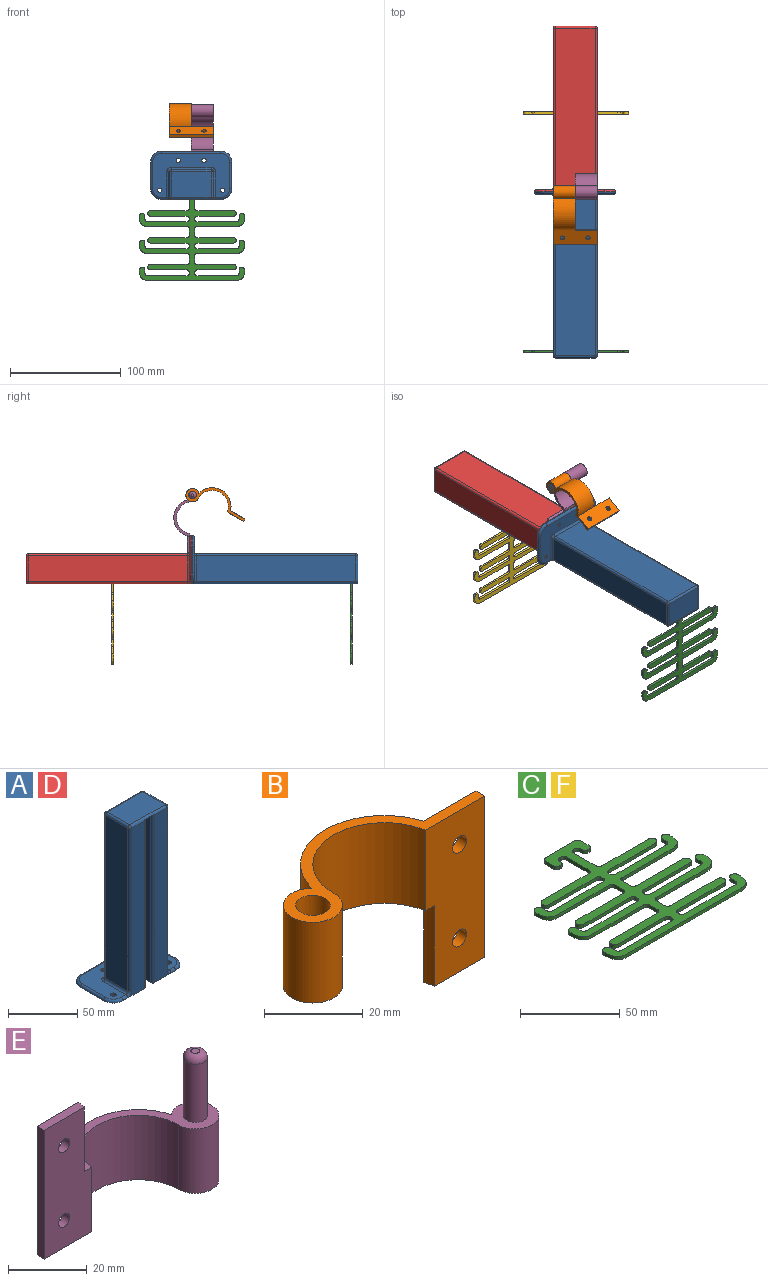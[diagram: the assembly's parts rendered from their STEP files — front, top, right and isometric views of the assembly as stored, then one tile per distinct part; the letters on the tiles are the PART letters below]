
ASSEMBLY  parts=6 mates=5
PART A: 61 faces, bbox 75.1x45.4x151.9 mm
  f0: plane 148x16.75mm, normal (0,-1,0), area 1890.4mm2, adj f16,f29,f36,f44,f47
  f1: plane 148x16.75mm, normal (0,-1,0), area 1890.4mm2, adj f16,f23,f28,f31,f36
  f2: plane 148x2mm, normal (0,1,0), area 296mm2, adj f16,f21,f54,f55
  f3: plane 148x14mm, normal (1,0,0), area 2072mm2, adj f16,f21,f55,f56
  f4: plane 148x22.5mm, normal (0,-1,0), area 3330mm2, adj f16,f21,f56,f57
  f5: plane 148x14mm, normal (-1,0,0), area 2072mm2, adj f16,f21,f57,f58
  f6: plane 148x2mm, normal (0,1,0), area 296mm2, adj f16,f21,f58,f59
  f7: plane 148x6mm, normal (1,0,0), area 888mm2, adj f16,f21,f31,f53
  f8: plane 148x2mm, normal (-1,0,0), area 296mm2, adj f16,f21,f53,f54
  f9: plane 148x2mm, normal (1,0,0), area 296mm2, adj f16,f21,f59,f60
  f10: plane 148x6mm, normal (-1,0,0), area 888mm2, adj f16,f21,f29,f60
  f11: cylinder r=2mm len=4mm, axis (0,0,-1), area 25.1mm2, adj f15,f16
  f12: cylinder r=2mm len=4mm, axis (0,0,-1), area 25.1mm2, adj f15,f16
  f13: cylinder r=2mm len=4mm, axis (0,0,-1), area 25.1mm2, adj f15,f16
  f14: cylinder r=2mm len=4mm, axis (0,0,-1), area 25.1mm2, adj f15,f16
  f15: plane 69.5x39.75mm, normal (0,0,1), area 1476.3mm2, adj f11,f12,f13,f14,f27,f34,f35,f39
  f16: plane 73.5x43.75mm, normal (0,0,-1), area 2624.5mm2, adj f0,f1,f2,f3,f4,f5,f6,f7
  f17: plane 144x23mm, normal (-1,0,0), area 3312mm2, adj f23,f24,f26,f27
  f18: plane 144x23mm, normal (1,0,0), area 3312mm2, adj f37,f38,f44,f45
  f19: plane 144x36mm, normal (0,1,0), area 5184mm2, adj f25,f26,f38,f39
  f20: plane 36x23mm, normal (0,0,1), area 828mm2, adj f24,f25,f36,f37
  f21: plane 26.5x20mm, normal (0,0,-1), area 440.3mm2, adj f2,f3,f4,f5,f6,f7,f8,f9
  f22: sphere r=2mm, area 6.3mm2, adj f24,f25,f26
  f23: cylinder r=2mm len=144mm, axis (0,0,-1), area 452.4mm2, adj f1,f17,f28,f32
  f24: cylinder r=2mm len=23mm, axis (0,1,0), area 72.3mm2, adj f17,f20,f22,f32
  f25: cylinder r=2mm len=36mm, axis (1,0,0), area 113.1mm2, adj f19,f20,f22,f33
  f26: cylinder r=2mm len=144mm, axis (0,0,-1), area 452.4mm2, adj f17,f19,f22,f34
  f27: cylinder r=2mm len=23mm, axis (0,-1,0), area 72.3mm2, adj f15,f17,f28,f34
  f28: torus R=4mm, axis (0,-1,0), area 13.5mm2, adj f1,f23,f27,f35
  f29: cylinder r=2mm len=149mm, axis (0,0,-1), area 466.2mm2, adj f0,f10,f16,f30,f36
  f30: cylinder r=2mm len=8.5mm, axis (-1,0,0), area 15.1mm2, adj f21,f29,f31,f36
  f31: cylinder r=2mm len=149mm, axis (0,0,-1), area 466.2mm2, adj f1,f7,f16,f30,f36
  f32: sphere r=2mm, area 6.3mm2, adj f23,f24,f36
  f33: sphere r=2mm, area 6.3mm2, adj f25,f37,f38
  f34: torus R=4mm, axis (0,0,1), area 13.5mm2, adj f15,f26,f27,f39
  f35: cylinder r=2mm len=4.75mm, axis (-1,0,0), area 14.9mm2, adj f15,f16,f28,f40
  f36: cylinder r=2mm len=36mm, axis (-1,0,0), area 103.2mm2, adj f0,f1,f20,f29,f30,f31,f32,f41
  f37: cylinder r=2mm len=23mm, axis (0,-1,0), area 72.3mm2, adj f18,f20,f33,f41
  f38: cylinder r=2mm len=144mm, axis (0,0,-1), area 452.4mm2, adj f18,f19,f33,f42
  f39: cylinder r=2mm len=36mm, axis (-1,0,0), area 113.1mm2, adj f15,f19,f34,f42
  f40: torus R=8mm, axis (0,0,1), area 45.8mm2, adj f15,f16,f35,f43
  f41: sphere r=2mm, area 6.3mm2, adj f36,f37,f44
  f42: torus R=4mm, axis (0,0,1), area 13.5mm2, adj f15,f38,f39,f45
  f43: cylinder r=2mm len=23.75mm, axis (0,1,0), area 74.6mm2, adj f15,f16,f40,f46
  f44: cylinder r=2mm len=144mm, axis (0,0,-1), area 452.4mm2, adj f0,f18,f41,f47
  f45: cylinder r=2mm len=23mm, axis (0,1,0), area 72.3mm2, adj f15,f18,f42,f47
  f46: torus R=8mm, axis (0,0,1), area 45.8mm2, adj f15,f16,f43,f48
  f47: torus R=4mm, axis (0,-1,0), area 13.5mm2, adj f0,f44,f45,f49
  f48: cylinder r=2mm len=53.5mm, axis (1,0,0), area 168.1mm2, adj f15,f16,f46,f50
  f49: cylinder r=2mm len=4.75mm, axis (-1,0,0), area 14.9mm2, adj f15,f16,f47,f51
  f50: torus R=8mm, axis (0,0,1), area 45.8mm2, adj f15,f16,f48,f52
  f51: torus R=8mm, axis (0,0,1), area 45.8mm2, adj f15,f16,f49,f52
  f52: cylinder r=2mm len=23.75mm, axis (0,-1,0), area 74.6mm2, adj f15,f16,f50,f51
  f53: cylinder r=2mm len=148mm, axis (0,0,-1), area 929.9mm2, adj f7,f8,f16,f21
  f54: cylinder r=2mm len=148mm, axis (0,0,1), area 465mm2, adj f2,f8,f16,f21
  f55: cylinder r=2mm len=148mm, axis (0,0,1), area 465mm2, adj f2,f3,f16,f21
  f56: cylinder r=2mm len=148mm, axis (0,0,-1), area 465mm2, adj f3,f4,f16,f21
  f57: cylinder r=2mm len=148mm, axis (0,0,-1), area 465mm2, adj f4,f5,f16,f21
  f58: cylinder r=2mm len=148mm, axis (0,0,1), area 465mm2, adj f5,f6,f16,f21
  f59: cylinder r=2mm len=148mm, axis (0,0,1), area 465mm2, adj f6,f9,f16,f21
  f60: cylinder r=2mm len=148mm, axis (0,0,-1), area 929.9mm2, adj f9,f10,f16,f21
PART B: 13 faces, bbox 57.7x23x40 mm
  f0: cylinder r=6mm len=20mm, axis (0,0,1), area 655.2mm2, adj f1,f4,f5,f6
  f1: cylinder r=14.5mm len=28.78mm, axis (0,0,1), area 860.8mm2, adj f0,f2,f5,f6
  f2: plane 40x16.97mm, normal (0,-1,0), area 602.8mm2, adj f1,f5,f6,f7,f8,f10,f11,f12
  f3: cylinder r=3.5mm len=20mm, axis (0,0,1), area 439.8mm2, adj f5,f6
  f4: cylinder r=17mm len=32.67mm, axis (0,0,1), area 877.6mm2, adj f0,f5,f6,f9
  f5: plane 43.32x23mm, normal (0,0,-1), area 184.5mm2, adj f0,f1,f2,f3,f4,f7
  f6: plane 57.75x23mm, normal (0,0,1), area 221.2mm2, adj f0,f1,f2,f3,f4,f8,f9
  f7: cylinder r=17mm len=20mm, axis (0,0,1), area 51.3mm2, adj f2,f5,f9,f10
  f8: plane 40x2.5mm, normal (1,0,0), area 100mm2, adj f2,f6,f9,f10
  f9: plane 40x15mm, normal (0,1,0), area 574.9mm2, adj f4,f6,f7,f8,f10,f11,f12
  f10: plane 15x2.5mm, normal (0,0,-1), area 36.7mm2, adj f2,f7,f8,f9
  f11: cylinder r=2mm len=4mm, axis (0,-1,0), area 31.4mm2, adj f2,f9
  f12: cylinder r=2mm len=4mm, axis (0,-1,0), area 31.4mm2, adj f2,f9
PART C: 102 faces, bbox 95x88x2 mm
  f0: plane 2x1mm, normal (1,0,0), area 2mm2, adj f62,f63,f64,f101
  f1: plane 33x2mm, normal (0,-1,0), area 66mm2, adj f2,f62,f63,f64
  f2: cylinder r=2.5mm len=5mm, axis (0,0,-1), area 15.7mm2, adj f1,f3,f62,f63
  f3: plane 33x2mm, normal (0,1,0), area 66mm2, adj f2,f62,f63,f65
  f4: plane 6x2mm, normal (1,0,0), area 12mm2, adj f62,f63,f65,f66
  f5: extruded ~43x9.33mm, area 98.7mm2, adj f6,f62,f63,f66
  f6: cylinder r=2.5mm len=5mm, axis (0,0,-1), area 15.7mm2, adj f5,f7,f62,f63
  f7: plane 3x2mm, normal (-1,0,0), area 6mm2, adj f6,f62,f63,f67
  f8: plane 36x2mm, normal (0,1,0), area 72mm2, adj f62,f63,f67,f68
  f9: plane 2x1mm, normal (1,0,0), area 2mm2, adj f62,f63,f68,f69
  f10: plane 33x2mm, normal (0,-1,0), area 66mm2, adj f11,f62,f63,f69
  f11: cylinder r=2.5mm len=5mm, axis (0,0,-1), area 15.7mm2, adj f10,f12,f62,f63
  f12: plane 33x2mm, normal (0,1,0), area 66mm2, adj f11,f62,f63,f70
  f13: plane 6x2mm, normal (1,0,0), area 12mm2, adj f62,f63,f70,f71
  f14: extruded ~43x9.33mm, area 98.7mm2, adj f15,f62,f63,f71
  f15: cylinder r=2.5mm len=5mm, axis (0,0,-1), area 15.7mm2, adj f14,f16,f62,f63
  f16: plane 3x2mm, normal (-1,0,0), area 6mm2, adj f15,f62,f63,f72
  f17: plane 36x2mm, normal (0,1,0), area 72mm2, adj f62,f63,f72,f73
  f18: plane 2x1mm, normal (1,0,0), area 2mm2, adj f62,f63,f73,f74
  f19: plane 33x2mm, normal (0,-1,0), area 66mm2, adj f20,f62,f63,f74
  f20: cylinder r=2.5mm len=5mm, axis (0,0,-1), area 15.7mm2, adj f19,f21,f62,f63
  f21: plane 33x2mm, normal (0,1,0), area 66mm2, adj f20,f62,f63,f75
  f22: plane 16x2mm, normal (1,0,0), area 32mm2, adj f62,f63,f75,f76
  f23: plane 2x1mm, normal (0,-1,0), area 2mm2, adj f62,f63,f76,f77
  f24: plane 2x1mm, normal (-1,0,0), area 2mm2, adj f62,f63,f77,f78
  f25: plane 2x1mm, normal (0,-1,0), area 2mm2, adj f62,f63,f78,f79
  f26: plane 6x2mm, normal (1,0,0), area 12mm2, adj f62,f63,f79,f80
  f27: plane 21x2mm, normal (0,1,0), area 42mm2, adj f62,f63,f80,f81
  f28: plane 6x2mm, normal (-1,0,0), area 12mm2, adj f62,f63,f81,f82
  f29: plane 2x1mm, normal (0,-1,0), area 2mm2, adj f62,f63,f82,f83
  f30: plane 2x1mm, normal (1,0,0), area 2mm2, adj f62,f63,f83,f84
  f31: plane 2x1mm, normal (0,-1,0), area 2mm2, adj f62,f63,f84,f85
  f32: plane 16x2mm, normal (-1,0,0), area 32mm2, adj f62,f63,f85,f86
  f33: plane 33x2mm, normal (0,1,0), area 66mm2, adj f34,f62,f63,f86
  f34: cylinder r=2.5mm len=5mm, axis (0,0,-1), area 15.7mm2, adj f33,f35,f62,f63
  f35: plane 33x2mm, normal (0,-1,0), area 66mm2, adj f34,f62,f63,f87
  f36: plane 2x1mm, normal (-1,0,0), area 2mm2, adj f62,f63,f87,f88
  f37: plane 36x2mm, normal (0,1,0), area 72mm2, adj f62,f63,f88,f89
  f38: plane 3x2mm, normal (1,0,0), area 6mm2, adj f39,f62,f63,f89
  f39: cylinder r=2.5mm len=5mm, axis (0,0,-1), area 15.7mm2, adj f38,f40,f62,f63
  f40: extruded ~43x9.33mm, area 98.7mm2, adj f39,f62,f63,f90
  f41: plane 6x2mm, normal (-1,0,0), area 12mm2, adj f62,f63,f90,f91
  f42: plane 33x2mm, normal (0,1,0), area 66mm2, adj f43,f62,f63,f91
  f43: cylinder r=2.5mm len=5mm, axis (0,0,-1), area 15.7mm2, adj f42,f44,f62,f63
  f44: plane 33x2mm, normal (0,-1,0), area 66mm2, adj f43,f62,f63,f92
  f45: plane 2x1mm, normal (-1,0,0), area 2mm2, adj f62,f63,f92,f93
  f46: plane 36x2mm, normal (0,1,0), area 72mm2, adj f62,f63,f93,f94
  f47: plane 3x2mm, normal (1,0,0), area 6mm2, adj f48,f62,f63,f94
  f48: cylinder r=2.5mm len=5mm, axis (0,0,-1), area 15.7mm2, adj f47,f49,f62,f63
  f49: extruded ~43x9.33mm, area 98.7mm2, adj f48,f62,f63,f95
  f50: plane 6x2mm, normal (-1,0,0), area 12mm2, adj f62,f63,f95,f96
  f51: plane 33x2mm, normal (0,1,0), area 66mm2, adj f52,f62,f63,f96
  f52: cylinder r=2.5mm len=5mm, axis (0,0,-1), area 15.7mm2, adj f51,f53,f62,f63
  f53: plane 33x2mm, normal (0,-1,0), area 66mm2, adj f52,f62,f63,f97
  f54: plane 2x1mm, normal (-1,0,0), area 2mm2, adj f62,f63,f97,f98
  f55: plane 36x2mm, normal (0,1,0), area 72mm2, adj f62,f63,f98,f99
  f56: plane 3x2mm, normal (1,0,0), area 6mm2, adj f57,f62,f63,f99
  f57: cylinder r=2.5mm len=5mm, axis (0,0,-1), area 15.7mm2, adj f56,f58,f62,f63
  f58: extruded ~95x9.33mm, area 215.5mm2, adj f57,f59,f62,f63
  f59: cylinder r=2.5mm len=5mm, axis (0,0,-1), area 15.7mm2, adj f58,f60,f62,f63
  f60: plane 3x2mm, normal (-1,0,0), area 6mm2, adj f59,f62,f63,f100
  f61: plane 36x2mm, normal (0,1,0), area 72mm2, adj f62,f63,f100,f101
  f62: plane 95x87.99mm, normal (0,0,1), area 3035.9mm2, adj f0,f1,f2,f3,f4,f5,f6,f7
  f63: plane 95x87.99mm, normal (0,0,-1), area 3035.9mm2, adj f0,f1,f2,f3,f4,f5,f6,f7
  f64: cylinder r=2mm len=2mm, axis (0,0,1), area 6.3mm2, adj f0,f1,f62,f63
  f65: cylinder r=2mm len=2mm, axis (0,0,-1), area 6.3mm2, adj f3,f4,f62,f63
  f66: cylinder r=2mm len=2mm, axis (0,0,-1), area 6.3mm2, adj f4,f5,f62,f63
  f67: cylinder r=2mm len=2mm, axis (0,0,1), area 6.3mm2, adj f7,f8,f62,f63
  f68: cylinder r=2mm len=2mm, axis (0,0,1), area 6.3mm2, adj f8,f9,f62,f63
  f69: cylinder r=2mm len=2mm, axis (0,0,1), area 6.3mm2, adj f9,f10,f62,f63
  f70: cylinder r=2mm len=2mm, axis (0,0,-1), area 6.3mm2, adj f12,f13,f62,f63
  f71: cylinder r=2mm len=2mm, axis (0,0,-1), area 6.3mm2, adj f13,f14,f62,f63
  f72: cylinder r=2mm len=2mm, axis (0,0,1), area 6.3mm2, adj f16,f17,f62,f63
  f73: cylinder r=2mm len=2mm, axis (0,0,1), area 6.3mm2, adj f17,f18,f62,f63
  f74: cylinder r=2mm len=2mm, axis (0,0,1), area 6.3mm2, adj f18,f19,f62,f63
  f75: cylinder r=2mm len=2mm, axis (0,0,1), area 6.3mm2, adj f21,f22,f62,f63
  f76: cylinder r=2mm len=2mm, axis (0,0,1), area 6.3mm2, adj f22,f23,f62,f63
  f77: cylinder r=2mm len=2mm, axis (0,0,1), area 6.3mm2, adj f23,f24,f62,f63
  f78: cylinder r=2mm len=2mm, axis (0,0,-1), area 6.3mm2, adj f24,f25,f62,f63
  f79: cylinder r=2mm len=2mm, axis (0,0,-1), area 6.3mm2, adj f25,f26,f62,f63
  f80: cylinder r=2mm len=2mm, axis (0,0,-1), area 6.3mm2, adj f26,f27,f62,f63
  f81: cylinder r=2mm len=2mm, axis (0,0,-1), area 6.3mm2, adj f27,f28,f62,f63
  f82: cylinder r=2mm len=2mm, axis (0,0,-1), area 6.3mm2, adj f28,f29,f62,f63
  f83: cylinder r=2mm len=2mm, axis (0,0,-1), area 6.3mm2, adj f29,f30,f62,f63
  f84: cylinder r=2mm len=2mm, axis (0,0,1), area 6.3mm2, adj f30,f31,f62,f63
  f85: cylinder r=2mm len=2mm, axis (0,0,1), area 6.3mm2, adj f31,f32,f62,f63
  f86: cylinder r=2mm len=2mm, axis (0,0,1), area 6.3mm2, adj f32,f33,f62,f63
  f87: cylinder r=2mm len=2mm, axis (0,0,-1), area 6.3mm2, adj f35,f36,f62,f63
  f88: cylinder r=2mm len=2mm, axis (0,0,1), area 6.3mm2, adj f36,f37,f62,f63
  f89: cylinder r=2mm len=2mm, axis (0,0,1), area 6.3mm2, adj f37,f38,f62,f63
  f90: cylinder r=2mm len=2mm, axis (0,0,-1), area 6.3mm2, adj f40,f41,f62,f63
  f91: cylinder r=2mm len=2mm, axis (0,0,1), area 6.3mm2, adj f41,f42,f62,f63
  f92: cylinder r=2mm len=2mm, axis (0,0,-1), area 6.3mm2, adj f44,f45,f62,f63
  f93: cylinder r=2mm len=2mm, axis (0,0,1), area 6.3mm2, adj f45,f46,f62,f63
  f94: cylinder r=2mm len=2mm, axis (0,0,1), area 6.3mm2, adj f46,f47,f62,f63
  f95: cylinder r=2mm len=2mm, axis (0,0,-1), area 6.3mm2, adj f49,f50,f62,f63
  f96: cylinder r=2mm len=2mm, axis (0,0,1), area 6.3mm2, adj f50,f51,f62,f63
  f97: cylinder r=2mm len=2mm, axis (0,0,-1), area 6.3mm2, adj f53,f54,f62,f63
  f98: cylinder r=2mm len=2mm, axis (0,0,1), area 6.3mm2, adj f54,f55,f62,f63
  f99: cylinder r=2mm len=2mm, axis (0,0,1), area 6.3mm2, adj f55,f56,f62,f63
  f100: cylinder r=2mm len=2mm, axis (0,0,1), area 6.3mm2, adj f60,f61,f62,f63
  f101: cylinder r=2mm len=2mm, axis (0,0,1), area 6.3mm2, adj f0,f61,f62,f63
PART D: same geometry as A
PART E: 15 faces, bbox 57.7x23x40 mm
  f0: cylinder r=17mm len=32.67mm, axis (0,0,-1), area 877.6mm2, adj f3,f6,f7,f9
  f1: cylinder r=3.1mm len=18mm, axis (0,0,-1), area 350.6mm2, adj f6,f12
  f2: plane 2.2x2.2mm, normal (0,0,1), area 3.8mm2, adj f12
  f3: cylinder r=6mm len=20mm, axis (0,0,-1), area 655.2mm2, adj f0,f5,f6,f7
  f4: plane 40x16.97mm, normal (0,-1,0), area 602.8mm2, adj f5,f6,f7,f8,f10,f11,f13,f14
  f5: cylinder r=14.5mm len=28.78mm, axis (0,0,-1), area 860.8mm2, adj f3,f4,f6,f7
  f6: plane 43.32x23mm, normal (0,0,1), area 192.8mm2, adj f0,f1,f3,f4,f5,f8
  f7: plane 57.75x23mm, normal (0,0,-1), area 259.7mm2, adj f0,f3,f4,f5,f9,f10
  f8: cylinder r=17mm len=20mm, axis (0,0,-1), area 51.3mm2, adj f4,f6,f9,f11
  f9: plane 40x15mm, normal (0,1,0), area 574.9mm2, adj f0,f7,f8,f10,f11,f13,f14
  f10: plane 40x2.5mm, normal (-1,0,0), area 100mm2, adj f4,f7,f9,f11
  f11: plane 15x2.5mm, normal (0,0,1), area 36.7mm2, adj f4,f8,f9,f10
  f12: torus R=1.1mm, axis (0,0,1), area 46.8mm2, adj f1,f2
  f13: cylinder r=2mm len=4mm, axis (0,-1,0), area 31.4mm2, adj f4,f9
  f14: cylinder r=2mm len=4mm, axis (0,-1,0), area 31.4mm2, adj f4,f9
PART F: same geometry as C
PLACE A rot(axis=(1,0,0),90deg) t=(-136.25,-2,-126.15)mm
PLACE B rot(axis=(0.65,-0.38,-0.65),138.6deg) t=(-40,3.56,55.25)mm
PLACE C rot(axis=(0,-0.71,-0.71),180deg) t=(97,-147,-101.15)mm
PLACE D rot(axis=(0,0.71,0.71),180deg) t=(96.25,-2,-126.15)mm
PLACE E rot(axis=(0,-1,0),90deg) t=(0,-2.5,58.75)mm
PLACE F rot(axis=(1,0,0),90deg) t=(-135.5,70.5,-101.15)mm
MATE cylindrical B.f0 <-> E.f3  axis (1,0,0) through (-20,-2.5,51.75)mm
MATE slider F.f63 <-> D.f16  axis (0,1,0) through (-16.75,70.5,-20.16)mm
MATE slider D.f16 <-> A.f16  axis (0,-1,0) through (-14.75,-2,-28.16)mm
MATE fastened E.f14 <-> D.f13  axis (0,-1,0) through (-8.38,0,7.22)mm
MATE slider C.f63 <-> D.f16  axis (0,-1,0) through (-16.75,-147,-20.16)mm
